# Revit family: Mailboxes_4C-Salsbury_Industries-Front_Load-6_Door_High_Units
name_source: partatom
category: Specialty Equipment
revit_build: Autodesk Revit 2016 (Build: 20190507_1515(x64)
units: mm (PartAtom-declared; Revit-internal decimal feet)

## family parameters
Cut with Voids When Loaded = No
Host = Face
OmniClass Number = 23.40.90.14.11
OmniClass Title = Mail Boxes
Part Type = Normal
Room Calculation Point = No
Round Connector Dimension = Use Diameter
Shared = No

## types (7) — shared parameters
Assembly Code = C1030910
Assembly Description = Mailboxes
Back Enclosure Material = Aluminum Alloy - Salsbury Finish - Clear (No finish)
Center Divider Offset = 14.381"
Depth = 16.450"
Door Depth = 0.190"
Door Slot R3 = 3700 Series 4C Door Configurations : Empty
Height = 23.875"
Lock Material = Stainless Steel - Salsbury Finish -  Polished
Manufacturer = Salsbury Industries
MasterFormat Number = 10 55 00
MasterFormat Title = Postal Specialties
OmniClass 23 Number = 23.40.90.14.11
OmniClass 23 Title = Mail Boxes
Rough Opening - Height = 22.625"
Type Comments = 4C Standard Horizontal Mailbox - Front Loading
URL = www.mailboxes.com
Version = 5.0 (01/01/21)

## per-type parameters (varying)
| type | Bottom Back Plate | Center Extrusion Offset | Decals | Description | Door Slot L1 | Door Slot L2 | Door Slot L3 | Door Slot L4 | Door Slot L5 | Door Slot L6 | Door Slot R1 | Door Slot R2 | Door Slot R4 | Door Slot R5 | Door Slot R6 | Double Wide Hidden Components | Left Inside Wall | Right Inside Wall | Rough Opening - Width | Top Back Plate | Vertical Center Divider | Width |
| 3706S-04 FL | No | 0.350" | Polycarbonate Film - Salsbury Finish - White | 6 Door High Unit: 4 MB1, OM2 | 3700 Series 4C Door Configurations : Empty | 3700 Series 4C Door Configurations : Empty | 3700 Series 4C Door Configurations : Empty | 3700 Series 4C Door Configurations : Empty | 3700 Series 4C Door Configurations : Empty | 3700 Series 4C Door Configurations : Empty | 3700 Series 4C Door Configurations : MB1 Door | 3700 Series 4C Door Configurations : MB1 Door w/ Divider | 3700 Series 4C OM2 Configuration : OM2-FL | 3700 Series 4C Door Configurations : MB1 Door w/ Divider | 3700 Series 4C Door Configurations : MB1 Door w/ Divider | No | No | No | 15.750" | No | No | 16.966" |
| 3706D-09 FL | Yes | 0.000" | Polycarbonate Film - Salsbury Finish - White | 6 Door High Unit: 9 MB1, OM3 | 3700 Series 4C Door Configurations : MB1 Door | 3700 Series 4C Door Configurations : MB1 Door w/ Divider | 3700 Series 4C Door Configurations : MB1 Door w/ Divider | 3700 Series 4C Door Configurations : MB1 Door w/ Divider | 3700 Series 4C Door Configurations : MB1 Door w/ Divider | 3700 Series 4C Door Configurations : MB1 Door w/ Divider | 3700 Series 4C Door Configurations : MB1 Door | 3700 Series 4C Door Configurations : MB1 Door w/ Divider | 3700 Series 4C OM2 Configuration : OM2-FL | 3700 Series Non_Operational Door Panel : Non-Operational door | 3700 Series 4C Door Configurations : MB1 Door w/ Divider | Yes | Yes | Yes | 29.875" | Yes | Yes | 31.097" |
| 3706D-2P FL | Yes | 0.000" | Plastic | 6 Door High Unit: 2 PL6 | 3700 Series 4C Door Configurations : Empty | 3700 Series 4C Door Configurations : Empty | 3700 Series 4C Door Configurations : Empty | 3700 Series 4C Door Configurations : Empty | 3700 Series 4C Door Configurations : Empty | 3700 Series 4C Parcel Configurations : PL6 | 3700 Series 4C Door Configurations : Empty | 3700 Series 4C Door Configurations : Empty | 3700 Series 4C Door Configurations : Empty | 3700 Series 4C Door Configurations : Empty | 3700 Series 4C Parcel Configurations : PL6 | Yes | Yes | Yes | 29.875" | Yes | Yes | 31.097" |
| 3706D-10 FL | Yes | 0.000" | Polycarbonate Film - Salsbury Finish - White | 6 Door High Unit: 10 MB1, OM2 | 3700 Series 4C Door Configurations : MB1 Door | 3700 Series 4C Door Configurations : MB1 Door w/ Divider | 3700 Series 4C Door Configurations : MB1 Door w/ Divider | 3700 Series 4C Door Configurations : MB1 Door w/ Divider | 3700 Series 4C Door Configurations : MB1 Door w/ Divider | 3700 Series 4C Door Configurations : MB1 Door w/ Divider | 3700 Series 4C Door Configurations : MB1 Door | 3700 Series 4C Door Configurations : MB1 Door w/ Divider | 3700 Series 4C OM2 Configuration : OM2-FL | 3700 Series 4C Door Configurations : MB1 Door w/ Divider | 3700 Series 4C Door Configurations : MB1 Door w/ Divider | Yes | Yes | Yes | 29.875" | Yes | Yes | 31.097" |
| 3706S-03 FL | No | 0.350" | Polycarbonate Film - Salsbury Finish - White | 6 Door High Unit: 3 MB1, OM3 | 3700 Series 4C Door Configurations : Empty | 3700 Series 4C Door Configurations : Empty | 3700 Series 4C Door Configurations : Empty | 3700 Series 4C Door Configurations : Empty | 3700 Series 4C Door Configurations : Empty | 3700 Series 4C Door Configurations : Empty | 3700 Series 4C Door Configurations : MB1 Door | 3700 Series 4C Door Configurations : MB1 Door w/ Divider | 3700 Series 4C OM2 Configuration : OM2-FL | 3700 Series Non_Operational Door Panel : Non-Operational door | 3700 Series 4C Door Configurations : MB1 Door w/ Divider | No | No | No | 15.750" | No | No | 16.966" |
| 3706S-1P FL | No | 0.350" | Polycarbonate Film - Salsbury Finish - White | 6 Door High Unit: 1 PL6 | 3700 Series 4C Door Configurations : Empty | 3700 Series 4C Door Configurations : Empty | 3700 Series 4C Door Configurations : Empty | 3700 Series 4C Door Configurations : Empty | 3700 Series 4C Door Configurations : Empty | 3700 Series 4C Door Configurations : Empty | 3700 Series 4C Door Configurations : Empty | 3700 Series 4C Door Configurations : Empty | 3700 Series 4C Door Configurations : Empty | 3700 Series 4C Door Configurations : Empty | 3700 Series 4C Parcel Configurations : PL6 | No | No | No | 15.750" | No | No | 16.966" |
| 3706D-05 FL | Yes | 0.000" | Polycarbonate Film - Salsbury Finish - White | 6 Door High Unit: 5 MB1, 1 PL5, OM2 | 3700 Series 4C Door Configurations : MB1 Door | 3700 Series 4C Door Configurations : Empty | 3700 Series 4C Door Configurations : Empty | 3700 Series 4C Door Configurations : Empty | 3700 Series 4C Door Configurations : Empty | 3700 Series 4C Parcel Configurations : PL5 w/ Divider | 3700 Series 4C Door Configurations : MB1 Door | 3700 Series 4C Door Configurations : MB1 Door w/ Divider | 3700 Series 4C OM2 Configuration : OM2-FL | 3700 Series 4C Door Configurations : MB1 Door w/ Divider | 3700 Series 4C Door Configurations : MB1 Door w/ Divider | Yes | Yes | Yes | 29.875" | Yes | Yes | 31.097" |

note: column(s) folded — value = type name in every type: Model

## geometry (parser evidence)
native form markers: Blend x2, Sweep x27
no freeform markers — native parametric forms only
